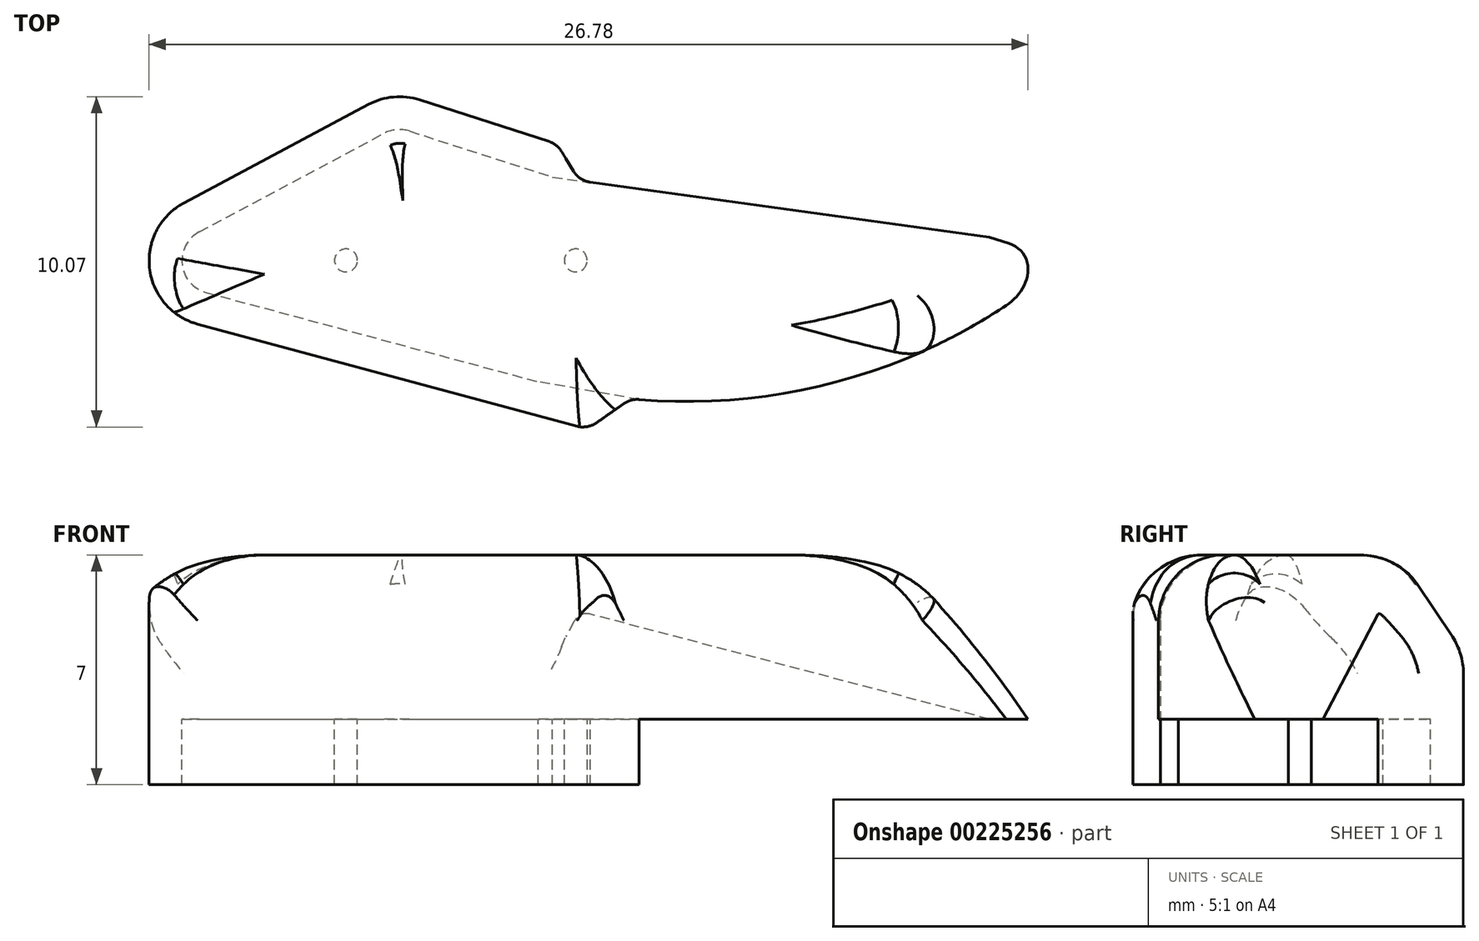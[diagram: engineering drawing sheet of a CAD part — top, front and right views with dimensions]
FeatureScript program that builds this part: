
annotation { "Feature Type Name" : "Feature", "Feature Type Description" : "" }
export const myFeature = defineFeature(function(context is Context, id is Id, definition is map)
    precondition{}
    {
        {
            var Q0;
            Q0=qCreatedBy(makeId("Top.planeOp"),FACE);
            var sketch = newSketch(context, id + "F0", { "sketchPlane" : qUnion([Q0])});
            skPoint(sketch, "E0", {"position": v(5, 0) * mm});
            skPoint(sketch, "E1", {"position": v(10, 0) * mm});
            skLineSegment(sketch, "E2", {"start": v(-4.97, 0) * mm, "end": v(6.33, 0) * mm, "construction": true});
            skCircle(sketch, "E3", {"center": v(5, 0) * mm, "radius": 0.35 * mm});
            skCircle(sketch, "E4", {"center": v(10, 0) * mm, "radius": 0.35 * mm});
            skLineSegment(sketch, "E5", {"start": v(0.74, -0.98) * mm, "end": v(10.85, -3.7) * mm});
            skLineSegment(sketch, "E6", {"start": v(0.53, 0.87) * mm, "end": v(6.16, 3.87) * mm});
            skPoint(sketch, "E7.visualSharp", {"position": v(-1.7, -0.32) * mm});
            skArc(sketch, "E7.filletArc", {"start": v(0.53, 0.87) * mm, "mid": v(0, -0.12) * mm, "end": v(0.74, -0.98) * mm});
            skLineSegment(sketch, "E8", {"start": v(6.93, 3.94) * mm, "end": v(11.29, 2.54) * mm});
            skPoint(sketch, "E9.visualSharp", {"position": v(6.53, 4.07) * mm});
            skArc(sketch, "E9.filletArc", {"start": v(6.93, 3.94) * mm, "mid": v(6.54, 3.99) * mm, "end": v(6.16, 3.87) * mm});
            skLineSegment(sketch, "E10", {"start": v(12.44, 2.38) * mm, "end": v(25, 0.66) * mm});
            skArc(sketch, "E11", {"start": v(13.93, -4.24) * mm, "mid": v(19.95, -3.7) * mm, "end": v(25.44, -1.15) * mm});
            skPoint(sketch, "E12.visualSharp", {"position": v(27.3, 0.34) * mm});
            skArc(sketch, "E12.filletArc", {"start": v(25.44, -1.15) * mm, "mid": v(25.84, -0.1) * mm, "end": v(25, 0.66) * mm});
            skLineSegment(sketch, "E13.0", {"start": v(7.24, 4.9) * mm, "end": v(11.18, 3.63) * mm});
            skLineSegment(sketch, "E13.1", {"start": v(0.48, -1.94) * mm, "end": v(12.04, -5.06) * mm});
            skArc(sketch, "E13.2", {"start": v(0.06, 1.75) * mm, "mid": v(-0.99, -0.24) * mm, "end": v(0.48, -1.94) * mm});
            skLineSegment(sketch, "E13.3", {"start": v(0.06, 1.75) * mm, "end": v(5.69, 4.76) * mm});
            skArc(sketch, "E13.4", {"start": v(7.24, 4.9) * mm, "mid": v(6.45, 4.98) * mm, "end": v(5.69, 4.76) * mm});
            skLineSegment(sketch, "E14", {"start": v(11.57, 3.32) * mm, "end": v(11.94, 2.71) * mm});
            skLineSegment(sketch, "E15", {"start": v(12.63, -4.95) * mm, "end": v(13.47, -4.36) * mm});
            skPoint(sketch, "E16.visualSharp", {"position": v(11.6, 3.5) * mm});
            skArc(sketch, "E16.filletArc", {"start": v(11.57, 3.32) * mm, "mid": v(11.4, 3.5) * mm, "end": v(11.18, 3.63) * mm});
            skPoint(sketch, "E17.visualSharp", {"position": v(11.29, 2.54) * mm});
            skArc(sketch, "E17.filletArc", {"start": v(11.94, 2.71) * mm, "mid": v(12.15, 2.5) * mm, "end": v(12.44, 2.38) * mm});
            skPoint(sketch, "E18.visualSharp", {"position": v(10.85, -3.7) * mm});
            skArc(sketch, "E18.filletArc", {"start": v(13.93, -4.24) * mm, "mid": v(13.69, -4.26) * mm, "end": v(13.47, -4.36) * mm});
            skPoint(sketch, "E19.visualSharp", {"position": v(10.46, -4.63) * mm});
            skArc(sketch, "E19.filletArc", {"start": v(12.04, -5.06) * mm, "mid": v(12.35, -5.07) * mm, "end": v(12.63, -4.95) * mm});
            skLineSegment(sketch, "E20", {"start": v(11.29, 2.54) * mm, "end": v(12.44, 2.38) * mm});
            skLineSegment(sketch, "E21", {"start": v(13.93, -4.24) * mm, "end": v(10.85, -3.7) * mm});
            skCircle(sketch, "E22", {"center": v(12, 0) * mm, "radius": 0.35 * mm});
            skSolve(sketch);
        }
        {
            var Q0;
            Q0 = qSketchRegion(id + "F0", true);
            var Q1;
            Q1=makeQuery(id+"F0.imprint","IMPRINT",FACE,{"disambiguationData":[TD([[makeQuery(id+"F0.imprint","IMPRINT",EDGE,{"derivedFrom":sQuery(id+"F0.wireOp",EDGE,"E3")}),1.0]])]});
            var Q2;
            Q2=makeQuery(id+"F0.imprint","IMPRINT",FACE,{"disambiguationData":[TD([[makeQuery(id+"F0.imprint","IMPRINT",EDGE,{"derivedFrom":sQuery(id+"F0.wireOp",EDGE,"E4")}),1.0]])]});
            var Q3;
            Q3=makeQuery(id+"F0.imprint","IMPRINT",FACE,{"disambiguationData":[TD([[makeQuery(id+"F0.imprint","IMPRINT",EDGE,{"derivedFrom":sQuery(id+"F0.wireOp",EDGE,"E22")}),1.0]])]});
            extrude(context, id + "F1", {"entities" : qUnion([Q0, Q1, Q2, Q3]), "depth" : 5 * mm, "offsetDistance" : 25 * mm});
        }
        {
            var Q0;
            Q0=makeQuery(id+"F1.opExtrude","CAP_EDGE",EDGE,{"disambiguationData":[OSD([sQuery(id+"F0.wireOp",EDGE,"E13.3")])],"isStart":false});
            var Q1;
            Q1=makeQuery(id+"F1.opExtrude","CAP_EDGE",EDGE,{"disambiguationData":[OSD([sQuery(id+"F0.wireOp",EDGE,"E13.0")])],"isStart":false});
            var Q2;
            Q2=makeQuery(id+"F1.opExtrude","CAP_EDGE",EDGE,{"disambiguationData":[OSD([sQuery(id+"F0.wireOp",EDGE,"E13.4")])],"isStart":false});
            chamfer(context, id + "F2", {"entities" : qUnion([Q0, Q1, Q2]), "chamferType" : ChamferType.TWO_OFFSETS, "width1" : 3 * mm, "oppositeDirection" : false, "width2" : 2 * mm});
        }
        {
            var Q0;
            {var subQ0=sQuery(id+"F0.wireOp",EDGE,"E13.3");Q0=makeQuery(id+"F2.opChamfer","BLEND_EDGE",EDGE,{"blendedFrom":[makeQuery(id+"F1.opExtrude","CAP_EDGE",EDGE,{"disambiguationData":[OSD([subQ0])],"isStart":false}),makeQuery(id+"F1.opExtrude","CAP_FACE",FACE,{"disambiguationData":[OSD([sQuery(id+"F0.wireOp",EDGE,"E10"),sQuery(id+"F0.wireOp",EDGE,"E11"),sQuery(id+"F0.wireOp",EDGE,"E12.filletArc"),sQuery(id+"F0.wireOp",EDGE,"E13.0"),sQuery(id+"F0.wireOp",EDGE,"E13.1"),sQuery(id+"F0.wireOp",EDGE,"E13.2"),subQ0,sQuery(id+"F0.wireOp",EDGE,"E13.4"),sQuery(id+"F0.wireOp",EDGE,"E14"),sQuery(id+"F0.wireOp",EDGE,"E15"),sQuery(id+"F0.wireOp",EDGE,"E16.filletArc"),sQuery(id+"F0.wireOp",EDGE,"E17.filletArc"),sQuery(id+"F0.wireOp",EDGE,"E18.filletArc"),sQuery(id+"F0.wireOp",EDGE,"E19.filletArc")])],"isStart":false})],"blendedInto":[makeQuery(id+"F1.opExtrude","CAP_FACE",FACE,{"disambiguationData":[OSD([sQuery(id+"F0.wireOp",EDGE,"E10"),sQuery(id+"F0.wireOp",EDGE,"E11"),sQuery(id+"F0.wireOp",EDGE,"E12.filletArc"),sQuery(id+"F0.wireOp",EDGE,"E13.0"),sQuery(id+"F0.wireOp",EDGE,"E13.1"),sQuery(id+"F0.wireOp",EDGE,"E13.2"),subQ0,sQuery(id+"F0.wireOp",EDGE,"E13.4"),sQuery(id+"F0.wireOp",EDGE,"E14"),sQuery(id+"F0.wireOp",EDGE,"E15"),sQuery(id+"F0.wireOp",EDGE,"E16.filletArc"),sQuery(id+"F0.wireOp",EDGE,"E17.filletArc"),sQuery(id+"F0.wireOp",EDGE,"E18.filletArc"),sQuery(id+"F0.wireOp",EDGE,"E19.filletArc")])],"isStart":false})]});}
            var Q1;
            {var subQ0=sQuery(id+"F0.wireOp",EDGE,"E13.0");Q1=makeQuery(id+"F2.opChamfer","BLEND_EDGE",EDGE,{"blendedFrom":[makeQuery(id+"F1.opExtrude","CAP_EDGE",EDGE,{"disambiguationData":[OSD([subQ0])],"isStart":false}),makeQuery(id+"F1.opExtrude","CAP_FACE",FACE,{"disambiguationData":[OSD([sQuery(id+"F0.wireOp",EDGE,"E10"),sQuery(id+"F0.wireOp",EDGE,"E11"),sQuery(id+"F0.wireOp",EDGE,"E12.filletArc"),subQ0,sQuery(id+"F0.wireOp",EDGE,"E13.1"),sQuery(id+"F0.wireOp",EDGE,"E13.2"),sQuery(id+"F0.wireOp",EDGE,"E13.3"),sQuery(id+"F0.wireOp",EDGE,"E13.4"),sQuery(id+"F0.wireOp",EDGE,"E14"),sQuery(id+"F0.wireOp",EDGE,"E15"),sQuery(id+"F0.wireOp",EDGE,"E16.filletArc"),sQuery(id+"F0.wireOp",EDGE,"E17.filletArc"),sQuery(id+"F0.wireOp",EDGE,"E18.filletArc"),sQuery(id+"F0.wireOp",EDGE,"E19.filletArc")])],"isStart":false})],"blendedInto":[makeQuery(id+"F1.opExtrude","CAP_FACE",FACE,{"disambiguationData":[OSD([sQuery(id+"F0.wireOp",EDGE,"E10"),sQuery(id+"F0.wireOp",EDGE,"E11"),sQuery(id+"F0.wireOp",EDGE,"E12.filletArc"),subQ0,sQuery(id+"F0.wireOp",EDGE,"E13.1"),sQuery(id+"F0.wireOp",EDGE,"E13.2"),sQuery(id+"F0.wireOp",EDGE,"E13.3"),sQuery(id+"F0.wireOp",EDGE,"E13.4"),sQuery(id+"F0.wireOp",EDGE,"E14"),sQuery(id+"F0.wireOp",EDGE,"E15"),sQuery(id+"F0.wireOp",EDGE,"E16.filletArc"),sQuery(id+"F0.wireOp",EDGE,"E17.filletArc"),sQuery(id+"F0.wireOp",EDGE,"E18.filletArc"),sQuery(id+"F0.wireOp",EDGE,"E19.filletArc")])],"isStart":false})]});}
            fillet(context, id + "F3", {"entities" : qUnion([Q0, Q1]), "radius" : 2 * mm, "tangentPropagation" : true, "allowEdgeOverflow" : false});
        }
        {
            var Q0;
            {var subQ0=sQuery(id+"F0.wireOp",EDGE,"E13.3");Q0=makeQuery(id+"F2.opChamfer","BLEND_EDGE",EDGE,{"blendedFrom":[makeQuery(id+"F1.opExtrude","CAP_EDGE",EDGE,{"disambiguationData":[OSD([subQ0])],"isStart":false}),makeQuery(id+"F1.opExtrude","SWEPT_FACE",FACE,{"disambiguationData":[OSD([subQ0])]})],"blendedInto":[makeQuery(id+"F1.opExtrude","SWEPT_FACE",FACE,{"disambiguationData":[OSD([subQ0])]})]});}
            var Q1;
            {var subQ0=sQuery(id+"F0.wireOp",EDGE,"E13.4");Q1=makeQuery(id+"F2.opChamfer","BLEND_EDGE",EDGE,{"blendedFrom":[makeQuery(id+"F1.opExtrude","CAP_EDGE",EDGE,{"disambiguationData":[OSD([subQ0])],"isStart":false}),makeQuery(id+"F1.opExtrude","SWEPT_FACE",FACE,{"disambiguationData":[OSD([subQ0])]})],"blendedInto":[makeQuery(id+"F1.opExtrude","SWEPT_FACE",FACE,{"disambiguationData":[OSD([subQ0])]})]});}
            fillet(context, id + "F4", {"entities" : qUnion([Q0, Q1]), "radius" : 2 * mm, "allowEdgeOverflow" : false});
        }
        {
            var Q0;
            Q0=makeQuery(id+"F1.opExtrude","CAP_EDGE",EDGE,{"disambiguationData":[OSD([sQuery(id+"F0.wireOp",EDGE,"E13.1")])],"isStart":false});
            fillet(context, id + "F5", {"entities" : qUnion([Q0]), "radius" : 2 * mm, "allowEdgeOverflow" : false});
        }
        {
            var Q0;
            Q0=makeQuery(id+"F5.opFillet","BLEND_EDGE",EDGE,{"blendedFrom":[makeQuery(id+"F1.opExtrude","CAP_EDGE",EDGE,{"disambiguationData":[OSD([sQuery(id+"F0.wireOp",EDGE,"E13.1")])],"isStart":false}),makeQuery(id+"F1.opExtrude","SWEPT_FACE",FACE,{"disambiguationData":[OSD([sQuery(id+"F0.wireOp",EDGE,"E11")])]})],"blendedInto":[makeQuery(id+"F1.opExtrude","SWEPT_FACE",FACE,{"disambiguationData":[OSD([sQuery(id+"F0.wireOp",EDGE,"E11")])]})]});
            var Q1;
            Q1=makeQuery(id+"F1.opExtrude","CAP_EDGE",EDGE,{"disambiguationData":[OSD([sQuery(id+"F0.wireOp",EDGE,"E11")])],"isStart":false});
            fillet(context, id + "F6", {"entities" : qUnion([Q0, Q1]), "radius" : 2 * mm, "allowEdgeOverflow" : false});
        }
        {
            var Q0;
            Q0=makeQuery(id+"F6.opFillet","BLEND_EDGE",EDGE,{"blendedFrom":[makeQuery(id+"F1.opExtrude","CAP_EDGE",EDGE,{"disambiguationData":[OSD([sQuery(id+"F0.wireOp",EDGE,"E11")])],"isStart":false}),makeQuery(id+"F5.opFillet","BLEND_FACE",FACE,{"disambiguationData":[OSD([sQuery(id+"F0.wireOp",EDGE,"E13.1")])]})],"blendedInto":[makeQuery(id+"F5.opFillet","BLEND_FACE",FACE,{"disambiguationData":[OSD([sQuery(id+"F0.wireOp",EDGE,"E13.1")])]})]});
            var Q1;
            {var subQ0=sQuery(id+"F0.wireOp",EDGE,"E19.filletArc");var subQ1=sQuery(id+"F0.wireOp",EDGE,"E18.filletArc");var subQ2=sQuery(id+"F0.wireOp",EDGE,"E17.filletArc");var subQ3=sQuery(id+"F0.wireOp",EDGE,"E16.filletArc");var subQ4=sQuery(id+"F0.wireOp",EDGE,"E15");var subQ5=sQuery(id+"F0.wireOp",EDGE,"E14");var subQ6=sQuery(id+"F0.wireOp",EDGE,"E13.4");var subQ7=sQuery(id+"F0.wireOp",EDGE,"E13.3");var subQ8=sQuery(id+"F0.wireOp",EDGE,"E13.2");var subQ9=sQuery(id+"F0.wireOp",EDGE,"E13.1");var subQ10=sQuery(id+"F0.wireOp",EDGE,"E13.0");var subQ11=sQuery(id+"F0.wireOp",EDGE,"E12.filletArc");var subQ12=sQuery(id+"F0.wireOp",EDGE,"E11");var subQ13=sQuery(id+"F0.wireOp",EDGE,"E10");Q1=makeQuery(id+"F5.opFillet","BLEND_EDGE",EDGE,{"blendedFrom":[makeQuery(id+"F1.opExtrude","CAP_EDGE",EDGE,{"disambiguationData":[OSD([subQ9])],"isStart":false}),makeQuery(id+"F3.opFillet","BLEND_FACE",FACE,{"disambiguationData":[OSD([subQ13,subQ12,subQ11,subQ10,subQ9,subQ8,subQ7,subQ6,subQ5,subQ4,subQ3,subQ2,subQ1,subQ0]),TDD([makeQuery(id+"F2.opChamfer","BLEND_EDGE",EDGE,{"blendedFrom":[makeQuery(id+"F1.opExtrude","CAP_EDGE",EDGE,{"disambiguationData":[OSD([subQ7])],"isStart":false}),makeQuery(id+"F1.opExtrude","CAP_FACE",FACE,{"disambiguationData":[OSD([subQ13,subQ12,subQ11,subQ10,subQ9,subQ8,subQ7,subQ6,subQ5,subQ4,subQ3,subQ2,subQ1,subQ0])],"isStart":false})],"blendedInto":[makeQuery(id+"F1.opExtrude","CAP_FACE",FACE,{"disambiguationData":[OSD([subQ13,subQ12,subQ11,subQ10,subQ9,subQ8,subQ7,subQ6,subQ5,subQ4,subQ3,subQ2,subQ1,subQ0])],"isStart":false})]})]),OD(1.0)]})],"blendedInto":[makeQuery(id+"F3.opFillet","BLEND_FACE",FACE,{"disambiguationData":[OSD([subQ13,subQ12,subQ11,subQ10,subQ9,subQ8,subQ7,subQ6,subQ5,subQ4,subQ3,subQ2,subQ1,subQ0]),TDD([makeQuery(id+"F2.opChamfer","BLEND_EDGE",EDGE,{"blendedFrom":[makeQuery(id+"F1.opExtrude","CAP_EDGE",EDGE,{"disambiguationData":[OSD([subQ7])],"isStart":false}),makeQuery(id+"F1.opExtrude","CAP_FACE",FACE,{"disambiguationData":[OSD([subQ13,subQ12,subQ11,subQ10,subQ9,subQ8,subQ7,subQ6,subQ5,subQ4,subQ3,subQ2,subQ1,subQ0])],"isStart":false})],"blendedInto":[makeQuery(id+"F1.opExtrude","CAP_FACE",FACE,{"disambiguationData":[OSD([subQ13,subQ12,subQ11,subQ10,subQ9,subQ8,subQ7,subQ6,subQ5,subQ4,subQ3,subQ2,subQ1,subQ0])],"isStart":false})]})]),OD(1.0)]})]});}
            var Q2;
            Q2=makeQuery(id+"F6.opFillet","BLEND_EDGE",EDGE,{"blendedFrom":[makeQuery(id+"F1.opExtrude","CAP_EDGE",EDGE,{"disambiguationData":[OSD([sQuery(id+"F0.wireOp",EDGE,"E11")])],"isStart":false}),makeQuery(id+"F2.opChamfer","BLEND_FACE",FACE,{"disambiguationData":[OSD([sQuery(id+"F0.wireOp",EDGE,"E13.0")])]})],"blendedInto":[makeQuery(id+"F2.opChamfer","BLEND_FACE",FACE,{"disambiguationData":[OSD([sQuery(id+"F0.wireOp",EDGE,"E13.0")])]})]});
            var Q3;
            {var subQ0=sQuery(id+"F0.wireOp",EDGE,"E19.filletArc");var subQ1=sQuery(id+"F0.wireOp",EDGE,"E18.filletArc");var subQ2=sQuery(id+"F0.wireOp",EDGE,"E17.filletArc");var subQ3=sQuery(id+"F0.wireOp",EDGE,"E16.filletArc");var subQ4=sQuery(id+"F0.wireOp",EDGE,"E15");var subQ5=sQuery(id+"F0.wireOp",EDGE,"E14");var subQ6=sQuery(id+"F0.wireOp",EDGE,"E13.4");var subQ7=sQuery(id+"F0.wireOp",EDGE,"E13.3");var subQ8=sQuery(id+"F0.wireOp",EDGE,"E13.2");var subQ9=sQuery(id+"F0.wireOp",EDGE,"E13.1");var subQ10=sQuery(id+"F0.wireOp",EDGE,"E13.0");var subQ11=sQuery(id+"F0.wireOp",EDGE,"E12.filletArc");var subQ12=sQuery(id+"F0.wireOp",EDGE,"E11");var subQ13=sQuery(id+"F0.wireOp",EDGE,"E10");Q3=makeQuery(id+"F6.opFillet","BLEND_EDGE",EDGE,{"blendedFrom":[makeQuery(id+"F1.opExtrude","CAP_EDGE",EDGE,{"disambiguationData":[OSD([subQ12])],"isStart":false}),makeQuery(id+"F3.opFillet","BLEND_FACE",FACE,{"disambiguationData":[OSD([subQ13,subQ12,subQ11,subQ10,subQ9,subQ8,subQ7,subQ6,subQ5,subQ4,subQ3,subQ2,subQ1,subQ0]),TDD([makeQuery(id+"F2.opChamfer","BLEND_EDGE",EDGE,{"blendedFrom":[makeQuery(id+"F1.opExtrude","CAP_EDGE",EDGE,{"disambiguationData":[OSD([subQ10])],"isStart":false}),makeQuery(id+"F1.opExtrude","CAP_FACE",FACE,{"disambiguationData":[OSD([subQ13,subQ12,subQ11,subQ10,subQ9,subQ8,subQ7,subQ6,subQ5,subQ4,subQ3,subQ2,subQ1,subQ0])],"isStart":false})],"blendedInto":[makeQuery(id+"F1.opExtrude","CAP_FACE",FACE,{"disambiguationData":[OSD([subQ13,subQ12,subQ11,subQ10,subQ9,subQ8,subQ7,subQ6,subQ5,subQ4,subQ3,subQ2,subQ1,subQ0])],"isStart":false})]})])]})],"blendedInto":[makeQuery(id+"F3.opFillet","BLEND_FACE",FACE,{"disambiguationData":[OSD([subQ13,subQ12,subQ11,subQ10,subQ9,subQ8,subQ7,subQ6,subQ5,subQ4,subQ3,subQ2,subQ1,subQ0]),TDD([makeQuery(id+"F2.opChamfer","BLEND_EDGE",EDGE,{"blendedFrom":[makeQuery(id+"F1.opExtrude","CAP_EDGE",EDGE,{"disambiguationData":[OSD([subQ10])],"isStart":false}),makeQuery(id+"F1.opExtrude","CAP_FACE",FACE,{"disambiguationData":[OSD([subQ13,subQ12,subQ11,subQ10,subQ9,subQ8,subQ7,subQ6,subQ5,subQ4,subQ3,subQ2,subQ1,subQ0])],"isStart":false})],"blendedInto":[makeQuery(id+"F1.opExtrude","CAP_FACE",FACE,{"disambiguationData":[OSD([subQ13,subQ12,subQ11,subQ10,subQ9,subQ8,subQ7,subQ6,subQ5,subQ4,subQ3,subQ2,subQ1,subQ0])],"isStart":false})]})])]})]});}
            fillet(context, id + "F7", {"entities" : qUnion([Q0, Q1, Q2, Q3]), "radius" : 1 * mm, "tangentPropagation" : true, "allowEdgeOverflow" : false});
        }
        {
            var Q0;
            Q0=makeQuery(id+"F0.imprint","IMPRINT",FACE,{"disambiguationData":[TD([[makeQuery(id+"F0.imprint","IMPRINT",EDGE,{"derivedFrom":sQuery(id+"F0.wireOp",EDGE,"E5")}),-1.0]])]});
            var Q1;
            Q1=makeQuery(id+"F0.imprint","IMPRINT",FACE,{"disambiguationData":[TD([[makeQuery(id+"F0.imprint","IMPRINT",EDGE,{"derivedFrom":sQuery(id+"F0.wireOp",EDGE,"E3")}),1.0]])]});
            var Q2;
            Q2=makeQuery(id+"F0.imprint","IMPRINT",FACE,{"disambiguationData":[TD([[makeQuery(id+"F0.imprint","IMPRINT",EDGE,{"derivedFrom":sQuery(id+"F0.wireOp",EDGE,"E22")}),1.0]])]});
            extrude(context, id + "F8", {"entities" : qUnion([Q0, Q1, Q2]), "operationType" : NewBodyOperationType.ADD, "oppositeDirection" : true, "depth" : 2 * mm, "offsetDistance" : 25 * mm});
        }
    });
